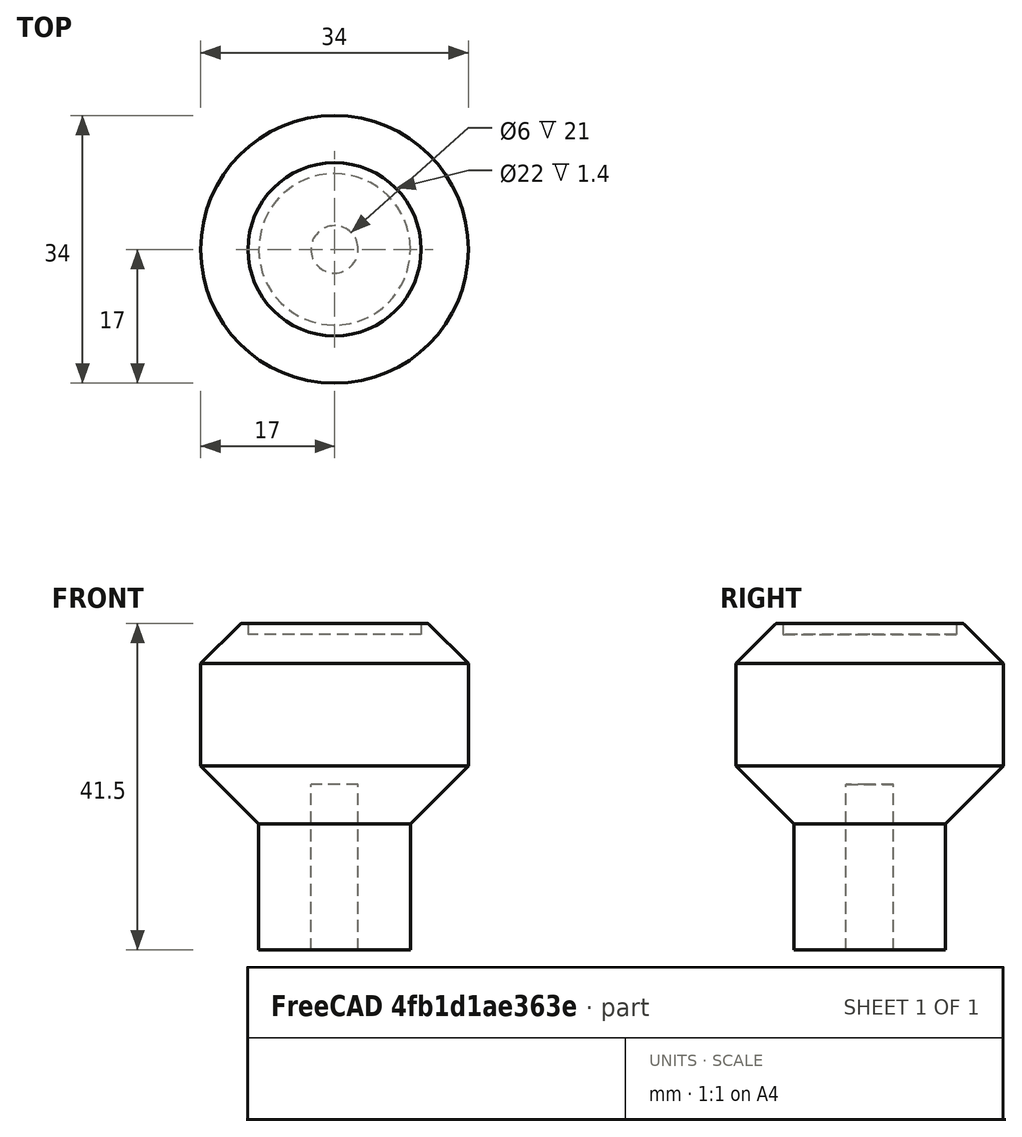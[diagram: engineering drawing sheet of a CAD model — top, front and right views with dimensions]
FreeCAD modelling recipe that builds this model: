
FCSTD DOCUMENT  (FreeCAD 0.16R6706 (Git))
Label: throttle_knob
License: All rights reserved
LicenseURL: http://en.wikipedia.org/wiki/All_rights_reserved
objects: Sketcher::SketchObject×1, PartDesign::Revolution×1
note: 3 computed .brp shape members not serialized (recipe doc carries the construction recipe); baked Part::Feature solids carry a one-line shape summary decoded from their .brp

FEATURE [Sketcher::SketchObject] Sketch  label="Sketch (profile)"
  Placement = pos=(0,0,0) rot=(-1,0,0;4.71239rad)
  expr: Constraints[27] = 22 / 2
  expr: Constraints[24] = 34 / 2
  expr: Constraints[21] = 19.25 / 2
  sketch-geometry (12):
    g0: LineSegment StartX=3 StartY=0 StartZ=0 EndX=3 EndY=21 EndZ=0
    g1: LineSegment StartX=3 StartY=0 StartZ=0 EndX=9.625 EndY=0 EndZ=0
    g2: LineSegment StartX=9.625 StartY=0 StartZ=0 EndX=9.625 EndY=16 EndZ=0
    g3: LineSegment StartX=9.625 StartY=16 StartZ=0 EndX=17 EndY=23.375 EndZ=0
    g4: LineSegment StartX=17 StartY=23.375 StartZ=0 EndX=17 EndY=36.375 EndZ=0
    g5: LineSegment StartX=17 StartY=36.375 StartZ=0 EndX=12.0214 EndY=41.3536 EndZ=0
    g6: LineSegment StartX=11.6679 StartY=41.5 StartZ=0 EndX=11 EndY=41.5 EndZ=0
    g7: LineSegment StartX=11 StartY=41.5 StartZ=0 EndX=11 EndY=40.1 EndZ=0
    g8: LineSegment StartX=11 StartY=40.1 StartZ=0 EndX=0 EndY=40.1 EndZ=0
    g9: LineSegment StartX=0 StartY=40.1 StartZ=0 EndX=0 EndY=21 EndZ=0
    g10: LineSegment StartX=0 StartY=21 StartZ=0 EndX=3 EndY=21 EndZ=0
    g11: ArcOfCircle CenterX=11.6679 CenterY=41 CenterZ=0 NormalX=0 NormalY=0 NormalZ=1 Radius=0.5 StartAngle=0.785398 EndAngle=1.5708
  constraints (35):
    c: PointOnObject(g0,g-1)
    c: Vertical(g0)
    c: Coincident(g1,g0)
    c: Horizontal(g1)
    c: Coincident(g2,g1)
    c: Vertical(g2)
    c: Coincident(g3,g2)
    c: Coincident(g4,g3)
    c: Vertical(g4)
    c: Coincident(g5,g4)
    c: Horizontal(g6)
    c: Coincident(g7,g6)
    c: Vertical(g7)
    c: Coincident(g8,g7)
    c: PointOnObject(g8,g-2)
    c: Horizontal(g8)
    c: Coincident(g9,g8)
    c: Vertical(g9)
    c: Coincident(g10,g9)
    c: Coincident(g10,g0)
    c: Horizontal(g10)
    c: DistanceX(g-1,g1) = 9.625
    c: DistanceY(g2,g2) = 16
    c: Angle(g3) = 0.785398
    c: DistanceX(g-1,g3) = 17
    c: DistanceY(g4,g4) = 13
    c: Angle(g5) = 2.35619
    c: DistanceX(g-1,g6) = 11
    c: DistanceY(g7,g7) = 1.4
    c: DistanceX(g10,g10) = 3
    c: DistanceY(g0,g0) = 21
    c: Tangent(g5,g11) = -1.5708
    c: Tangent(g6,g11) = -1.5708
    c: Radius(g11) = 0.5
    c: DistanceY(g-1,g6) = 41.5
FEATURE [PartDesign::Revolution] Revolution  label="Revolution (knob)"
  Angle = 360
  Axis = (0,0,1)
  Base = (0,0,0)
  Placement = pos=(0,0,0) rot=(-1,0,0;4.71239rad)
  ReferenceAxis = -> Sketch [V_Axis]
  Reversed = true
  Sketch = -> Sketch
